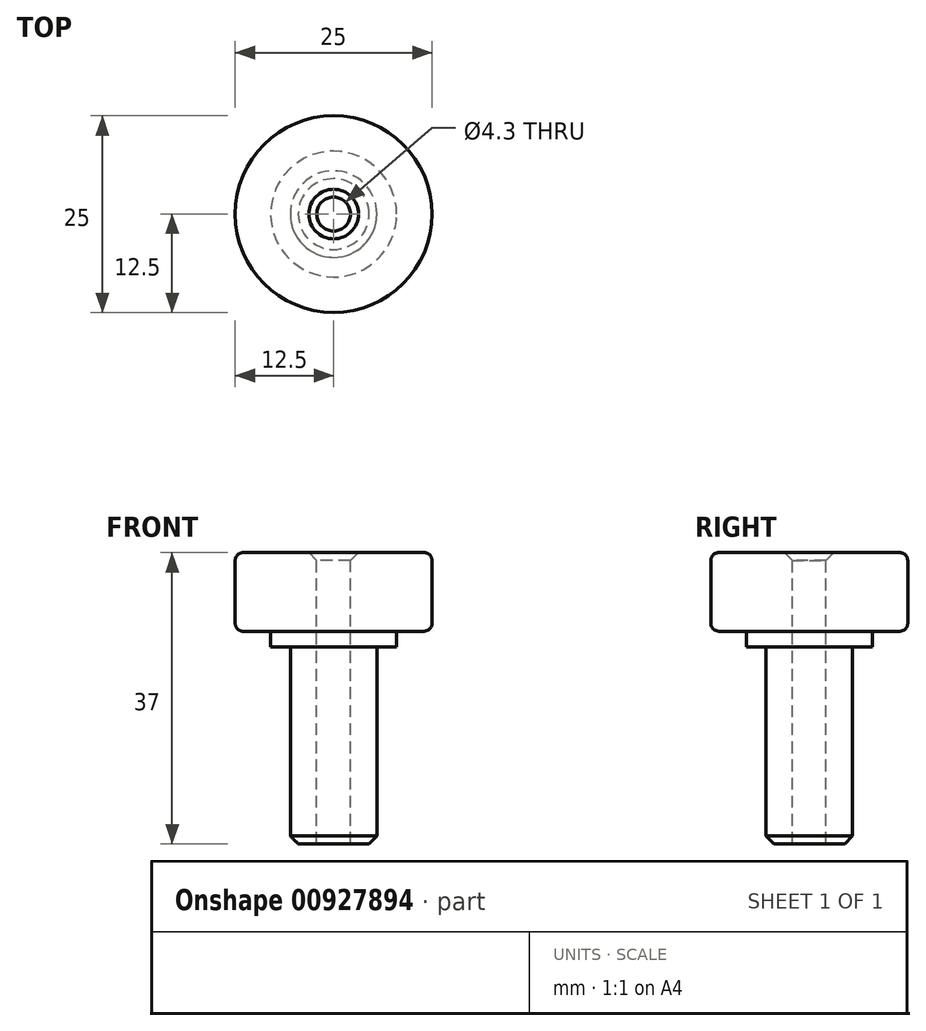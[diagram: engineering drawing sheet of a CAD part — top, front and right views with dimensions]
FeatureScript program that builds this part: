
annotation { "Feature Type Name" : "Feature", "Feature Type Description" : "" }
export const myFeature = defineFeature(function(context is Context, id is Id, definition is map)
    precondition{}
    {
        {
            var Q0;
            Q0=qCreatedBy(makeId("Front.planeOp"),FACE);
            var sketch = newSketch(context, id + "F0", { "sketchPlane" : qUnion([Q0])});
            skLineSegment(sketch, "E0", {"start": v(-2.15, 0) * mm, "end": v(-2.15, 37) * mm});
            skLineSegment(sketch, "E1", {"start": v(-2.15, 37) * mm, "end": v(-12.5, 37) * mm});
            skLineSegment(sketch, "E2", {"start": v(-12.5, 37) * mm, "end": v(-12.5, 27) * mm});
            skLineSegment(sketch, "E3", {"start": v(-12.5, 27) * mm, "end": v(-8, 27) * mm});
            skLineSegment(sketch, "E4", {"start": v(-8, 27) * mm, "end": v(-8, 25) * mm});
            skLineSegment(sketch, "E5", {"start": v(-8, 25) * mm, "end": v(-5.5, 25) * mm});
            skLineSegment(sketch, "E6", {"start": v(-5.5, 25) * mm, "end": v(-5.5, 0) * mm});
            skLineSegment(sketch, "E7", {"start": v(-5.5, 0) * mm, "end": v(-2.15, 0) * mm});
            skLineSegment(sketch, "E8", {"start": v(-2.15, 37) * mm, "end": v(0, 37) * mm, "construction": true});
            skLineSegment(sketch, "E9", {"start": v(0, 37) * mm, "end": v(0, 0) * mm, "construction": true});
            skLineSegment(sketch, "E10", {"start": v(0, 0) * mm, "end": v(-2.15, 0) * mm, "construction": true});
            skSolve(sketch);
        }
        {
            var Q0;
            Q0=makeQuery(id+"F0.imprint","IMPRINT",FACE,{"disambiguationData":[TD([[makeQuery(id+"F0.imprint","IMPRINT",EDGE,{"derivedFrom":sQuery(id+"F0.wireOp",EDGE,"E0")}),1.0]])]});
            var Q1;
            Q1=sQuery(id+"F0.wireOp",EDGE,"E9");
            revolve(context, id + "F1", {"surfaceOperationType" : NewSurfaceOperationType.NEW, "entities" : qUnion([Q0]), "axis" : qUnion([Q1]), "revolveType" : RevolveType.FULL});
        }
        {
            var Q0;
            Q0=makeQuery(id+"F1.opRevolve","SWEPT_EDGE",EDGE,{"disambiguationData":[OSD([sQuery(id+"F0.wireOp",EDGE,"E6"),sQuery(id+"F0.wireOp",EDGE,"E7")])]});
            var Q1;
            Q1=makeQuery(id+"F1.opRevolve","SWEPT_EDGE",EDGE,{"disambiguationData":[OSD([sQuery(id+"F0.wireOp",EDGE,"E0"),sQuery(id+"F0.wireOp",EDGE,"E1")])]});
            chamfer(context, id + "F2", {"entities" : qUnion([Q0, Q1]), "width" : 1 * mm, "tangentPropagation" : true});
        }
        {
            var Q0;
            Q0=makeQuery(id+"F1.opRevolve","SWEPT_EDGE",EDGE,{"disambiguationData":[OSD([sQuery(id+"F0.wireOp",EDGE,"E1"),sQuery(id+"F0.wireOp",EDGE,"E2")])]});
            var Q1;
            Q1=makeQuery(id+"F1.opRevolve","SWEPT_EDGE",EDGE,{"disambiguationData":[OSD([sQuery(id+"F0.wireOp",EDGE,"E2"),sQuery(id+"F0.wireOp",EDGE,"E3")])]});
            fillet(context, id + "F3", {"entities" : qUnion([Q0, Q1]), "radius" : 1 * mm, "tangentPropagation" : true, "allowEdgeOverflow" : false});
        }
    });
